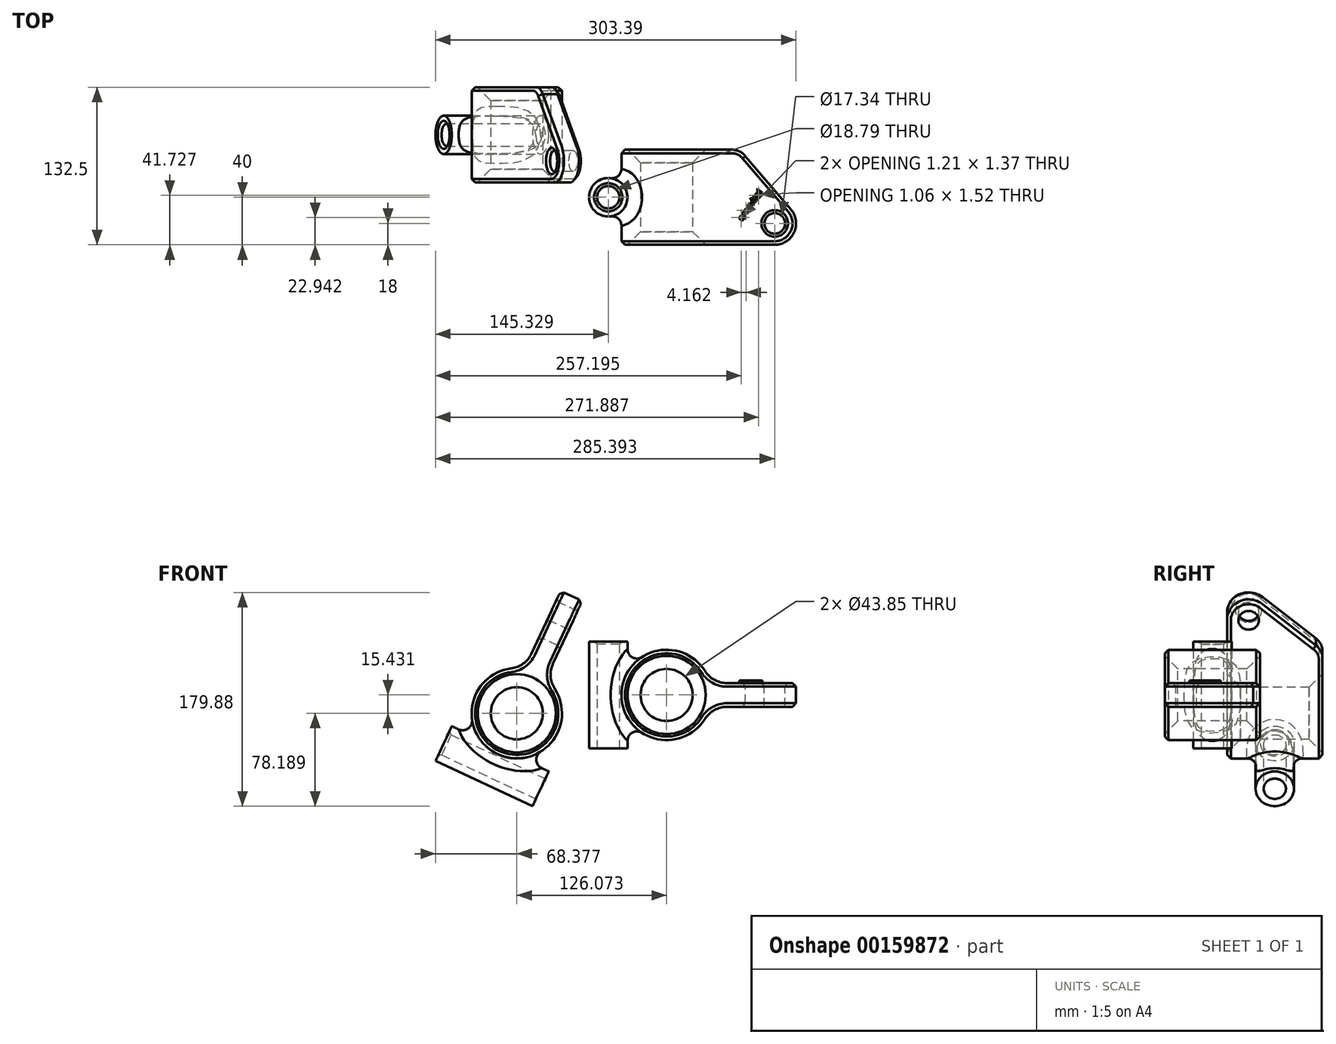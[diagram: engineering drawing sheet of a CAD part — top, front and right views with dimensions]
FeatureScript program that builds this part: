
annotation { "Feature Type Name" : "Feature", "Feature Type Description" : "" }
export const myFeature = defineFeature(function(context is Context, id is Id, definition is map)
    precondition{}
    {
        {
            var Q0;
            Q0=qCreatedBy(makeId("Front.planeOp"),FACE);
            var sketch = newSketch(context, id + "F0", { "sketchPlane" : qUnion([Q0])});
            skArc(sketch, "E0", {"start": v(32.14, 20.27) * mm, "mid": v(-38, 0) * mm, "end": v(32.14, -20.27) * mm});
            skCircle(sketch, "E1", {"center": v(0, 0) * mm, "radius": 21.92 * mm});
            skLineSegment(sketch, "E2", {"start": v(50.75, 10) * mm, "end": v(108.94, 10) * mm});
            skLineSegment(sketch, "E3", {"start": v(108.94, 10) * mm, "end": v(108.94, 0) * mm});
            skLineSegment(sketch, "E4.MirrorCS", {"start": v(50.75, -10) * mm, "end": v(108.94, -10) * mm});
            skLineSegment(sketch, "E5.MirrorCS", {"start": v(108.94, -10) * mm, "end": v(108.94, 0) * mm});
            skPoint(sketch, "E6.visualSharp", {"position": v(36.66, 10) * mm});
            skArc(sketch, "E6.filletArc", {"start": v(32.14, 20.27) * mm, "mid": v(40.13, 12.74) * mm, "end": v(50.75, 10) * mm});
            skPoint(sketch, "E7.visualSharp", {"position": v(36.66, -10) * mm});
            skArc(sketch, "E7.filletArc", {"start": v(50.75, -10) * mm, "mid": v(40.13, -12.74) * mm, "end": v(32.14, -20.27) * mm});
            skSolve(sketch);
        }
        {
            var Q0;
            Q0=makeQuery(id+"F0.imprint","IMPRINT",FACE,{"disambiguationData":[TD([[makeQuery(id+"F0.imprint","IMPRINT",EDGE,{"derivedFrom":sQuery(id+"F0.wireOp",EDGE,"E0")}),1.0]])]});
            extrude(context, id + "F1", {"entities" : qUnion([Q0]), "oppositeDirection" : true, "depth" : 80 * mm});
        }
        {
            var Q0;
            Q0=qCreatedBy(makeId("Top.planeOp"),FACE);
            var sketch = newSketch(context, id + "F2", { "sketchPlane" : qUnion([Q0])});
            skLineSegment(sketch, "E8", {"start": v(-38, 0) * mm, "end": v(-38, 80) * mm});
            skLineSegment(sketch, "E9", {"start": v(-38, 40) * mm, "end": v(-39.72, 40) * mm});
            skCircle(sketch, "E10", {"center": v(-49.12, 40) * mm, "radius": 16.16 * mm});
            skCircle(sketch, "E11", {"center": v(-49.12, 40) * mm, "radius": 9.4 * mm});
            skLineSegment(sketch, "E12.0.0", {"start": v(50.75, 0) * mm, "end": v(90.94, 0) * mm});
            skLineSegment(sketch, "E12.0.1", {"start": v(108.94, 18) * mm, "end": v(108.94, 80) * mm});
            skLineSegment(sketch, "E12.0.2", {"start": v(55.15, 80) * mm, "end": v(50.75, 80) * mm});
            skLineSegment(sketch, "E12.0.3", {"start": v(50.75, 80) * mm, "end": v(50.75, 0) * mm});
            skPoint(sketch, "E13.visualSharp", {"position": v(108.94, 0) * mm});
            skArc(sketch, "E13.filletArc", {"start": v(90.94, 0) * mm, "mid": v(103.67, 5.27) * mm, "end": v(108.94, 18) * mm});
            skArc(sketch, "E14.filletArc", {"start": v(66.32, 74.44) * mm, "mid": v(61.4, 78.53) * mm, "end": v(55.15, 80) * mm});
            skArc(sketch, "E15", {"start": v(90.94, 0) * mm, "mid": v(107.3, 10.47) * mm, "end": v(104.62, 29.7) * mm});
            skLineSegment(sketch, "E16", {"start": v(66.32, 74.44) * mm, "end": v(104.62, 29.7) * mm});
            skCircle(sketch, "E17", {"center": v(90.94, 18) * mm, "radius": 8.67 * mm});
            skLineSegment(sketch, "E18", {"start": v(108.94, 80) * mm, "end": v(50.75, 80) * mm});
            skLineSegment(sketch, "E19", {"start": v(108.94, 18) * mm, "end": v(108.94, 0) * mm});
            skLineSegment(sketch, "E20", {"start": v(90.94, 0) * mm, "end": v(108.94, 0) * mm});
            skSolve(sketch);
        }
        {
            var Q0;
            {var subQ2=sQuery(id+"F2.wireOp",EDGE,"E12.0.1");Q0=makeQuery(id+"F2.imprint","IMPRINT",FACE,{"disambiguationData":[TD([[makeQuery(id+"F2.imprint","IMPRINT",EDGE,{"derivedFrom":subQ2}),1.0]])]});}
            var Q1;
            {var subQ2=sQuery(id+"F2.wireOp",EDGE,"E19");Q1=makeQuery(id+"F2.imprint","IMPRINT",FACE,{"disambiguationData":[TD([[makeQuery(id+"F2.imprint","IMPRINT",EDGE,{"derivedFrom":subQ2}),-1.0]])]});}
            var Q2;
            Q2=makeQuery(id+"F2.imprint","IMPRINT",FACE,{"disambiguationData":[TD([[makeQuery(id+"F2.imprint","IMPRINT",EDGE,{"derivedFrom":sQuery(id+"F2.wireOp",EDGE,"E17")}),1.0]])]});
            extrude(context, id + "F3", {"entities" : qUnion([Q0, Q1, Q2]), "operationType" : NewBodyOperationType.REMOVE, "endBound" : BoundingType.THROUGH_ALL, "oppositeDirection" : true, "depth" : 25 * mm, "hasSecondDirection" : true, "secondDirectionOppositeDirection" : false, "secondDirectionDepth" : 25 * mm});
        }
        {
            var Q0;
            Q0=makeQuery(id+"F2.imprint","IMPRINT",FACE,{"disambiguationData":[TD([[makeQuery(id+"F2.imprint","IMPRINT",EDGE,{"derivedFrom":sQuery(id+"F2.wireOp",EDGE,"E11")}),-1.0]])]});
            var Q1;
            {var subQ0=sQuery(id+"F2.wireOp",EDGE,"E8");var subQ1=makeQuery(id+"F2.imprint","IMPRINT",VERTEX,{"derivedFrom":subQ0});Q1=makeQuery(id+"F2.imprint","IMPRINT",FACE,{"disambiguationData":[TD([[makeQuery(id+"F2.imprint","IMPRINT",EDGE,{"disambiguationData":[TD([[subQ1,1.0]])],"derivedFrom":subQ0}),-1.0]])]});}
            extrude(context, id + "F4", {"entities" : qUnion([Q0, Q1]), "operationType" : NewBodyOperationType.ADD, "depth" : 90 * mm, "symmetric" : true});
        }
        {
            var Q0;
            Q0=makeQuery(id+"F4.boolean.opBoolean","INTERSECT",EDGE,{"derivedFrom":[makeQuery(id+"F1.opExtrude","SWEPT_FACE",FACE,{"disambiguationData":[OSD([sQuery(id+"F0.wireOp",EDGE,"E0")])]}),makeQuery(id+"F4.opExtrude","SWEPT_FACE",FACE,{"disambiguationData":[OSD([sQuery(id+"F2.wireOp",EDGE,"E10")])]})]});
            fillet(context, id + "F5", {"entities" : qUnion([Q0]), "radius" : 8 * mm, "tangentPropagation" : true, "allowEdgeOverflow" : false});
        }
        {
            var Q0;
            Q0=makeQuery(id+"F1.opExtrude","CAP_EDGE",EDGE,{"disambiguationData":[OSD([sQuery(id+"F0.wireOp",EDGE,"E0")])],"isStart":true});
            var Q1;
            Q1=makeQuery(id+"F3.boolean.opBoolean","INTERSECT",EDGE,{"derivedFrom":[makeQuery(id+"F1.opExtrude","SWEPT_FACE",FACE,{"disambiguationData":[OSD([sQuery(id+"F0.wireOp",EDGE,"E2")])]}),makeQuery(id+"F3.opExtrude","SWEPT_FACE",FACE,{"disambiguationData":[OSD([sQuery(id+"F2.wireOp",EDGE,"E14.filletArc")])]})]});
            chamfer(context, id + "F6", {"entities" : qUnion([Q0, Q1]), "width" : 3 * mm, "tangentPropagation" : true});
        }
        {
            var Q0;
            Q0=makeQuery(id+"F1.opExtrude","SWEPT_FACE",FACE,{"disambiguationData":[OSD([sQuery(id+"F0.wireOp",EDGE,"E1")])]});
            chamfer(context, id + "F7", {"entities" : qUnion([Q0]), "width" : 11 * mm, "tangentPropagation" : true});
        }
        {
            var Q0;
            Q0=makeQuery(id+"F4.opExtrude","CAP_EDGE",EDGE,{"disambiguationData":[OSD([sQuery(id+"F2.wireOp",EDGE,"E11")])],"isStart":false});
            var Q1;
            Q1=makeQuery(id+"F3.boolean.opBoolean","INTERSECT",EDGE,{"derivedFrom":[makeQuery(id+"F1.opExtrude","SWEPT_FACE",FACE,{"disambiguationData":[OSD([sQuery(id+"F0.wireOp",EDGE,"E2")])]}),makeQuery(id+"F3.opExtrude","SWEPT_FACE",FACE,{"disambiguationData":[OSD([sQuery(id+"F2.wireOp",EDGE,"E17")])]})]});
            chamfer(context, id + "F8", {"entities" : qUnion([Q0, Q1]), "width" : 2.5 * mm, "tangentPropagation" : true});
        }
        {
            var Q0;
            Q0=makeQuery(id+"F1.opExtrude","SWEPT_BODY",BODY,{"disambiguationData":[OSD([sQuery(id+"F0.wireOp",EDGE,"E0"),sQuery(id+"F0.wireOp",EDGE,"E1"),sQuery(id+"F0.wireOp",EDGE,"E2"),sQuery(id+"F0.wireOp",EDGE,"E3"),sQuery(id+"F0.wireOp",EDGE,"E4.MirrorCS"),sQuery(id+"F0.wireOp",EDGE,"E5.MirrorCS"),sQuery(id+"F0.wireOp",EDGE,"E6.filletArc"),sQuery(id+"F0.wireOp",EDGE,"E7.filletArc")])]});
            transform(context, id + "F9", {"entities" : qUnion([Q0]), "transformType" : TransformType.TRANSLATION_3D, "dx" : -190.5 * mm, "dy" : 0 * mm, "dz" : 2 * mm, "makeCopy" : true});
        }
        {
            var Q0;
            Q0=makeQuery(id+"F9.opPattern","COPY",BODY,{"derivedFrom":makeQuery(id+"F1.opExtrude","SWEPT_BODY",BODY,{"disambiguationData":[OSD([sQuery(id+"F0.wireOp",EDGE,"E0"),sQuery(id+"F0.wireOp",EDGE,"E1"),sQuery(id+"F0.wireOp",EDGE,"E2"),sQuery(id+"F0.wireOp",EDGE,"E3"),sQuery(id+"F0.wireOp",EDGE,"E4.MirrorCS"),sQuery(id+"F0.wireOp",EDGE,"E5.MirrorCS"),sQuery(id+"F0.wireOp",EDGE,"E6.filletArc"),sQuery(id+"F0.wireOp",EDGE,"E7.filletArc")])]}),"instanceName":"1"});
            var Q1;
            Q1=makeQuery(id+"F9.opPattern","COPY",EDGE,{"derivedFrom":makeQuery(id+"F1.opExtrude","SWEPT_EDGE",EDGE,{"disambiguationData":[OSD([sQuery(id+"F0.wireOp",EDGE,"E0"),sQuery(id+"F0.wireOp",EDGE,"E6.filletArc")])]}),"instanceName":"1"});
            transform(context, id + "F10", {"entities" : qUnion([Q0]), "transformType" : TransformType.ROTATION, "transformAxis" : qUnion([Q1]), "angle" : 65 * degree, "makeCopy" : false});
        }
        {
            var Q0;
            Q0=makeQuery(id+"F9.opPattern","COPY",BODY,{"derivedFrom":makeQuery(id+"F1.opExtrude","SWEPT_BODY",BODY,{"disambiguationData":[OSD([sQuery(id+"F0.wireOp",EDGE,"E0"),sQuery(id+"F0.wireOp",EDGE,"E1"),sQuery(id+"F0.wireOp",EDGE,"E2"),sQuery(id+"F0.wireOp",EDGE,"E3"),sQuery(id+"F0.wireOp",EDGE,"E4.MirrorCS"),sQuery(id+"F0.wireOp",EDGE,"E5.MirrorCS"),sQuery(id+"F0.wireOp",EDGE,"E6.filletArc"),sQuery(id+"F0.wireOp",EDGE,"E7.filletArc")])]}),"instanceName":"1"});
            var Q1;
            {var subQ0=sQuery(id+"F0.wireOp",EDGE,"E1");Q1=makeQuery(id+"F9.opPattern","COPY",EDGE,{"derivedFrom":makeQuery(id+"F7.opChamfer","BLEND_EDGE",EDGE,{"blendedFrom":[makeQuery(id+"F1.opExtrude","CAP_EDGE",EDGE,{"disambiguationData":[OSD([subQ0])],"isStart":true}),makeQuery(id+"F1.opExtrude","SWEPT_FACE",FACE,{"disambiguationData":[OSD([subQ0])]})],"blendedInto":[makeQuery(id+"F1.opExtrude","SWEPT_FACE",FACE,{"disambiguationData":[OSD([subQ0])]})]}),"instanceName":"1"});}
            var Q2;
            {var subQ0=makeQuery(id+"F1.opExtrude","SWEPT_FACE",FACE,{"disambiguationData":[OSD([sQuery(id+"F0.wireOp",EDGE,"E2")])]});Q2=makeQuery(id+"F9.opPattern","COPY",EDGE,{"derivedFrom":makeQuery(id+"F6.opChamfer","BLEND_EDGE",EDGE,{"blendedFrom":[makeQuery(id+"F3.boolean.opBoolean","INTERSECT",EDGE,{"derivedFrom":[subQ0,makeQuery(id+"F3.opExtrude","SWEPT_FACE",FACE,{"disambiguationData":[OSD([sQuery(id+"F2.wireOp",EDGE,"E16")])]})]}),subQ0],"blendedInto":[subQ0]}),"instanceName":"1"});}
            transform(context, id + "F11", {"entities" : qUnion([Q0]), "transformType" : TransformType.TRANSLATION_3D, "dx" : 27.5 * mm, "dy" : 52.5 * mm, "dz" : 0 * mm, "makeCopy" : false});
        }
        {
            var Q0;
            Q0=makeQuery(id+"F1.opExtrude","SWEPT_FACE",FACE,{"disambiguationData":[OSD([sQuery(id+"F0.wireOp",EDGE,"E2")])]});
            var sketch = newSketch(context, id + "F12", { "sketchPlane" : qUnion([Q0])});
            skText(sketch, "E21", { "text": "erezvital", "fontName": "OpenSans-Bold.ttf"});
            const initialGuessF12  = {"E21": [0.06363, 0.01979, 0.57358, 0.81915, 0.005]};
            skSetInitialGuess(sketch, initialGuessF12);
            skSolve(sketch);
        }
        {
            var Q0;
            Q0 = qSketchRegion(id + "F12", true);
            extrude(context, id + "F13", {"entities" : qUnion([Q0]), "depth" : 2 * mm});
        }
    });
